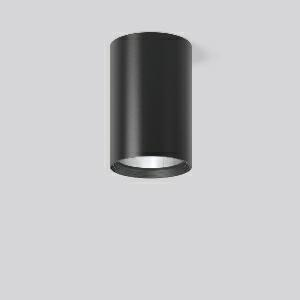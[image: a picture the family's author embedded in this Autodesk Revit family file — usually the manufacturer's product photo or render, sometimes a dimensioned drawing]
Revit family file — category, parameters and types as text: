
# Revit family: heledon_maxi_a_931223_003_1_1ae5
name_source: partatom
category: Lighting Fixtures
units: mm (PartAtom-declared; Revit-internal decimal feet)

## family parameters
Cut with Voids When Loaded = No
Host = Face
Light Source = No
Part Type = Normal
Room Calculation Point = No
Round Connector Dimension = Use Diameter
Shared = No

## types (1)
- HELEDON maxi A (1 x LED Modul 940, 4400 lm, 4000)
    Apparent Load = 35 VA
    Approval mark = CE
    CIE Flux Codes = 100 100 100 100 100
    Color Rendering = 92
    Color Temperature = 4000
    Default Elevation = 1800 mm
    Description = Series: HELEDON maxi
Cylindrical surface-mounted downlight. Housing: die-cast aluminium, powder-coated. Internal ceiling frame polycarbonate with bayonet mounting. Black plastic ring and recessed LED to prevent glare from the side. Optical assembly with reflector made of MIRO-Silver with 98% total light reflection for outstanding efficiency - can be changed without tools. Best colour rendering index Ra>90. Suitable for Ceiling mounting. Easy installation with a separate ceiling frame with bayonet mounting and plug connection. Driver integrated. Connected via plug-in connector. High quality converter without flickering and stroboscopic effect. The following accessories can be mounted without use of tools: interchangeable lenses, decorative glasses, honeycomb louvre, clear and frosted diffusers, white interchangeable plastic ring. 
Colour: deep black, matt (RAL 9005)
Diameter: 123 mm
Height: 183 mm
Lamp: LED
Socket: without socket
Colour temperature: 4000K
Colour rendering index (CRI): 92
System power: 35 W
Rated luminous flux: 4400 lm
Luminous efficiency: 126 lm/W
Control gear: Regulated power supply
Protection class: I
Type of protection: IP 20
    Height = 183 mm
    Lamp = 1 x LED Modul 940
    Lamp Light Flux = 4400 lm
    Lamp count = 1
    Length = 123 mm
    Lifetime = 50000 h
    Luminous efficacy = 126 lm/W
    Manufacturer = RZB
    ModVariant = No
    Model = 931223.003.1
    Mounting Place = Ceiling
    Mounting Type = Surface mounted
    Number of Poles = 1
    OnlyDefault = Yes
    Power Factor = 1
    Product Name = HELEDON maxi A
    Product group = Surface mounted downlights
    ProductGroupID = 302
    Protection Class = Protection class I
    Protection Degree = IP 20
    RLX_Detail_Level = 1
    RLX_Emergency_Light_Flux = 0 lm
    RLX_Emergency_Type = 0
    RLX_Emergency_Type_DB = No
    RlxData = <blob elided: 97185 chars, md5=a3d550e0>
    Socket = socket
    Standby Power = 0 W
    System Light Flux = 4400 lm
    System Power = 35 W
    Type Comments = Product without accessories
    Type Image = 931192.003.jpg
    URL = http://relux.com
    VarID = ---
    Voltage = 230 V
    Voltage Range = 220-240 V
    Weight = 0.00 kg
    Width = 0 mm  [stored 0 ft]

note: [stored X ft] marks values corroborated as IEEE doubles in the binary element streams (Revit-internal decimal feet)

## geometry (parser evidence)
native form markers: Blend x4, Sweep x10
no freeform markers — native parametric forms only
